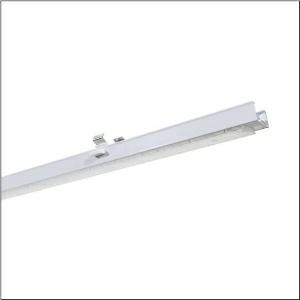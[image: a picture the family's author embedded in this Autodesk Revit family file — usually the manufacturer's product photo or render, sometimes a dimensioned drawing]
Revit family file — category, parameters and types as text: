
# Revit family: sanierungs-leuchteneinsatz_31_gen_2_51re18mb1cb_d366
name_source: partatom
category: Lighting Fixtures
units: mm (PartAtom-declared; Revit-internal decimal feet)

## family parameters
Cut with Voids When Loaded = No
Host = Face
Light Source = No
Part Type = Normal
Room Calculation Point = No
Round Connector Dimension = Use Diameter
Shared = No

## types (1)
- --- (1 x LED, 11500 lm, 66 W, 3500K)
    Apparent Load = 66 VA
    CIE Flux Codes = 71 89 97 97 100
    Color Rendering = 80
    Color Temperature = 3500K
    Default Elevation = 1800 mm
    Description = Refurbishment luminaire insert Gen.2, luminaire insert, of extruded aluminium section, coated, traffic white (RAL 9016), length: 1.472mm, width: 91mm, height: 53mm, LED rated luminous flux: 11.500lm, light colour: 835, control gear: ON/OFF Multilumen, with system connector: socket, mains connection: 220..240V, AC, 50/60Hz, luminous flux adjustable on luminaire in eight steps (3450/4380/5800/6700/8350/9200/10500/11500lm ), connected load according to luminous flux setting (19/24/32/37/47/52/60/66W), primary light control with lens, of plastic, primary optical cover: cover, of PMMA, light emission: direct distribution, protection rating (complete): IP20, insulation class (complete): insulation class I (protective earthing), certification: CE, UKCA, impact resistance: IK02, permissible ambient temperature for indoor applications: -20..+40°C, packaging unit: 1 piece
    Height = 58 mm
    Lamp = 1 x LED
    Lamp Light Flux = 11500 lm
    Lamp Power = 66 W
    Lamp count = 1
    Length = 1472 mm
    Luminous efficacy = 174 lm/W
    Manufacturer = Siteco
    ModVariant = No
    Model = 51RE18MB1CB
    Mounting Place = Ceiling
    Mounting Type = Pendant
    Number of Poles = 1
    OnlyDefault = Yes
    Power Factor = 1
    Product Name = Sanierungs-Leuchteneinsatz 31 Gen.2
    Product group = luminaire insert
    ProductGroupID = 902
    Protection Class = Protection class I
    Protection Degree = IP 20
    RLX_Detail_Level = 1
    RlxData = <blob elided: 21257 chars, md5=40b3bad2>
    Socket = socket
    Standby Power = 0 W
    System Light Flux = 11500 lm
    System Power = 66 W
    Type Comments = factory setting: luminous flux: 100 % | (ON | ON | ON)
    Type Image = l_1266702.jpg
    URL = http://relux.com
    VarID = @adj_049467
    Voltage = 0 V
    Weight = 0.00 kg
    Width = 65 mm

## geometry (parser evidence)
native form markers: Blend x4, Sweep x10
no freeform markers — native parametric forms only
